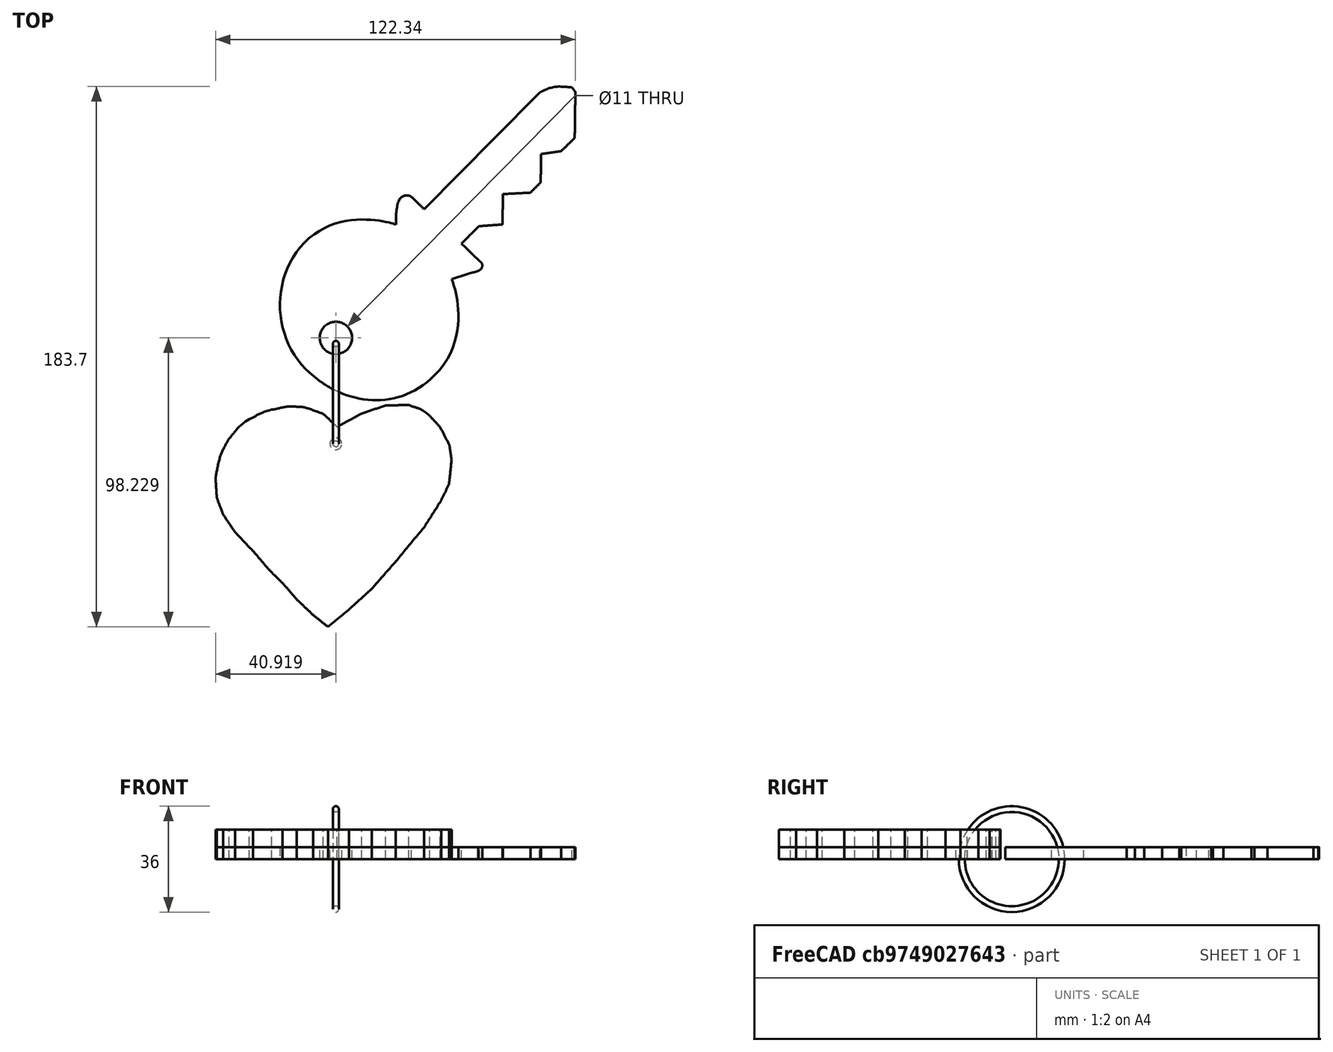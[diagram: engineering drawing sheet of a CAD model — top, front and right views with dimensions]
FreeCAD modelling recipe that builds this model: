
FCSTD DOCUMENT  (FreeCAD 0.14R3700 (Git))
Label: menudosC3
License: CC-BY 3.0
LicenseURL: http://creativecommons.org/licenses/by/3.0/
objects: Part::Extrusion×3, Part::Feature×3, Part::Cylinder×2, Part::Cut×2, Part::MultiCommon×1, Part::Compound×1, Part::Torus×1
note: 13 computed .brp shape members not serialized (recipe doc carries the construction recipe); baked Part::Feature solids carry a one-line shape summary decoded from their .brp

FEATURE [Part::Cylinder] Cylinder  label="Cilindro"
  Angle = 360
  Height = 20
  Placement = pos=(-1,28,-3) rot=(0,0,1;0rad)
  Radius = 2
FEATURE [Part::Extrusion] Extrude  label="corz4"
  Dir = (0,0,4)
  Placement = pos=(0,293,0) rot=(0,0,1;0rad)
  Solid = true
FEATURE [Part::Feature] mc
  Placement = pos=(-41,-35,2) rot=(0,0,1;0rad)
  shape: bbox 70.07 x 67.11 x 5.647 mm, 12857 faces, 0 solids (baked)
FEATURE [Part::Feature] path
  shape: bbox 80.25 x 75.48 x 2e-07 mm, 0 faces, 0 solids (baked)
FEATURE [Part::Extrusion] Extrude001  label="corazon10"
  Base = -> path
  Dir = (0,0,10)
  Placement = pos=(0,293,0) rot=(0,0,1;0rad)
  Solid = true
FEATURE [Part::Feature] Cut001  label="Cora10aguj"
  shape: bbox 80.25 x 75.48 x 10 mm, 33 faces (baked)
FEATURE [Part::MultiCommon] Common
  Shapes = -> [mc,Cut001]
FEATURE [Part::Cut] Cut
  Base = -> Extrude
  Tool = -> Cylinder
FEATURE [Part::Compound] Compound  label="LlaveroMenudosCorazones"
  Links = -> [Cut,Common]
FEATURE [Part::Cylinder] Cylinder001  label="Agujero-llave"
  Angle = 360
  Height = 10
  Placement = pos=(-41,0,-2) rot=(0,0,1;0rad)
  Radius = 5.5
FEATURE [Part::Extrusion] Extrude002  label="Contorno-llave"
  Dir = (0,0,4)
  Solid = true
FEATURE [Part::Cut] Cut002  label="Llave"
  Base = -> Extrude002
  Placement = pos=(28,93,0) rot=(0,0,1;0.785398rad)
  Tool = -> Cylinder001
FEATURE [Part::Torus] Torus  label="Anilla"
  Angle1 = -180
  Angle2 = 180
  Angle3 = 360
  Placement = pos=(-1,45,0) rot=(0,1,0;1.5708rad)
  Radius1 = 17
  Radius2 = 1
